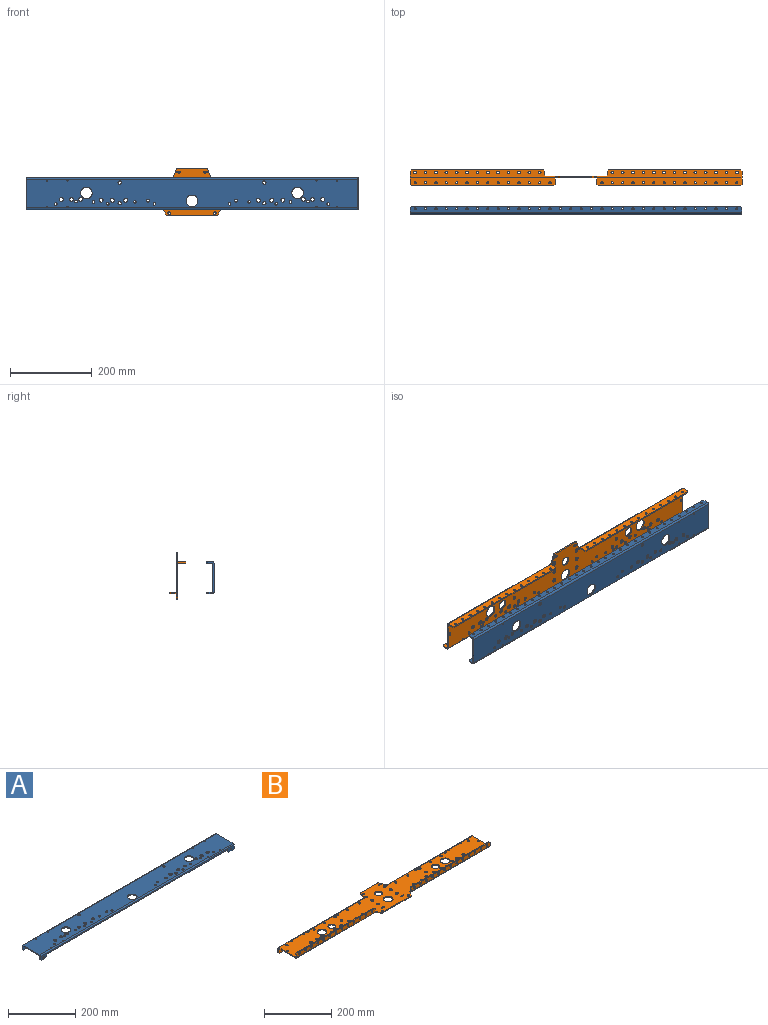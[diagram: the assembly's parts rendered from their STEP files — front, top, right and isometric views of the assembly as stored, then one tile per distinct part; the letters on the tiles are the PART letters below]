
ASSEMBLY  parts=2 mates=1
PART A: 101 faces, bbox 812.8x77.7x19.1 mm
  f0: cylinder r=4.06mm len=8.13mm, axis (0,0,1), area 81.1mm2, adj f83,f84
  f1: cylinder r=4.06mm len=8.13mm, axis (0,0,1), area 81.1mm2, adj f83,f84
  f2: cylinder r=4.06mm len=8.13mm, axis (0,0,1), area 81.1mm2, adj f83,f84
  f3: cylinder r=4.06mm len=8.13mm, axis (0,0,1), area 81.1mm2, adj f83,f84
  f4: cylinder r=3.38mm len=6.76mm, axis (0,0,1), area 67.4mm2, adj f83,f84
  f5: cylinder r=3.38mm len=6.76mm, axis (0,0,1), area 67.4mm2, adj f83,f84
  f6: cylinder r=3.38mm len=6.76mm, axis (0,0,1), area 67.4mm2, adj f83,f84
  f7: cylinder r=3.38mm len=6.76mm, axis (0,0,1), area 67.4mm2, adj f83,f84
  f8: cylinder r=3.35mm len=6.71mm, axis (0,0,1), area 66.9mm2, adj f83,f84
  f9: cylinder r=3.35mm len=6.71mm, axis (0,0,1), area 66.9mm2, adj f83,f84
  f10: cylinder r=3.35mm len=6.71mm, axis (0,0,1), area 66.9mm2, adj f83,f84
  f11: cylinder r=3.35mm len=6.71mm, axis (0,0,1), area 66.9mm2, adj f83,f84
  f12: cylinder r=3.35mm len=6.71mm, axis (0,0,1), area 66.9mm2, adj f83,f84
  f13: cylinder r=3.35mm len=6.71mm, axis (0,0,1), area 66.9mm2, adj f83,f84
  f14: cylinder r=3.35mm len=6.71mm, axis (0,0,1), area 66.9mm2, adj f83,f84
  f15: cylinder r=3.35mm len=6.71mm, axis (0,0,1), area 66.9mm2, adj f83,f84
  f16: cylinder r=3.35mm len=6.71mm, axis (0,0,1), area 66.9mm2, adj f83,f84
  f17: cylinder r=3.35mm len=6.71mm, axis (0,0,1), area 66.9mm2, adj f83,f84
  f18: cylinder r=14.29mm len=28.58mm, axis (0,0,1), area 285mm2, adj f83,f84
  f19: cylinder r=14.29mm len=28.58mm, axis (0,0,1), area 285mm2, adj f83,f84
  f20: cylinder r=1.27mm len=3.18mm, axis (0,0,1), area 25.3mm2, adj f83,f84
  f21: cylinder r=1.27mm len=3.18mm, axis (0,0,1), area 25.3mm2, adj f83,f84
  f22: cylinder r=1.27mm len=3.18mm, axis (0,0,1), area 25.3mm2, adj f83,f84
  f23: cylinder r=1.27mm len=3.18mm, axis (0,0,1), area 25.3mm2, adj f83,f84
  f24: cylinder r=1.27mm len=3.18mm, axis (0,0,1), area 25.3mm2, adj f83,f84
  f25: cylinder r=1.27mm len=3.18mm, axis (0,0,1), area 25.3mm2, adj f83,f84
  f26: cylinder r=1.27mm len=3.18mm, axis (0,0,1), area 25.3mm2, adj f83,f84
  f27: cylinder r=1.27mm len=3.18mm, axis (0,0,1), area 25.3mm2, adj f83,f84
  f28: cylinder r=4.83mm len=9.65mm, axis (0,0,1), area 96.3mm2, adj f83,f84
  f29: cylinder r=4.83mm len=9.65mm, axis (0,0,1), area 96.3mm2, adj f83,f84
  f30: cylinder r=4.83mm len=9.65mm, axis (0,0,1), area 96.3mm2, adj f83,f84
  f31: cylinder r=4.83mm len=9.65mm, axis (0,0,1), area 96.3mm2, adj f83,f84
  f32: cylinder r=4.83mm len=9.65mm, axis (0,0,1), area 96.3mm2, adj f83,f84
  f33: cylinder r=4.83mm len=9.65mm, axis (0,0,1), area 96.3mm2, adj f83,f84
  f34: cylinder r=4.83mm len=9.65mm, axis (0,0,1), area 96.3mm2, adj f83,f84
  f35: cylinder r=4.83mm len=9.65mm, axis (0,0,1), area 96.3mm2, adj f83,f84
  f36: cylinder r=4.83mm len=9.65mm, axis (0,0,1), area 96.3mm2, adj f83,f84
  f37: cylinder r=4.83mm len=9.65mm, axis (0,0,1), area 96.3mm2, adj f83,f84
  f38: cylinder r=4.83mm len=9.65mm, axis (0,0,1), area 96.3mm2, adj f83,f84
  f39: cylinder r=4.83mm len=9.65mm, axis (0,0,1), area 96.3mm2, adj f83,f84
  f40: cylinder r=2.67mm len=5.33mm, axis (0,1,0), area 53.2mm2, adj f75,f76
  f41: cylinder r=2.67mm len=5.33mm, axis (0,1,0), area 53.2mm2, adj f87,f88
  f42: cylinder r=2.67mm len=5.33mm, axis (0,1,0), area 53.2mm2, adj f87,f88
  f43: cylinder r=2.67mm len=5.33mm, axis (0,1,0), area 53.2mm2, adj f87,f88
  f44: cylinder r=2.67mm len=5.33mm, axis (0,1,0), area 53.2mm2, adj f87,f88
  f45: cylinder r=2.67mm len=5.33mm, axis (0,1,0), area 53.2mm2, adj f87,f88
  f46: cylinder r=2.67mm len=5.33mm, axis (0,1,0), area 53.2mm2, adj f87,f88
  f47: cylinder r=2.67mm len=5.33mm, axis (0,1,0), area 53.2mm2, adj f87,f88
  f48: cylinder r=2.67mm len=5.33mm, axis (0,1,0), area 53.2mm2, adj f87,f88
  f49: cylinder r=2.67mm len=5.33mm, axis (0,1,0), area 53.2mm2, adj f87,f88
  f50: cylinder r=2.67mm len=5.33mm, axis (0,1,0), area 53.2mm2, adj f87,f88
  f51: cylinder r=2.67mm len=5.33mm, axis (0,1,0), area 53.2mm2, adj f87,f88
  f52: cylinder r=2.67mm len=5.33mm, axis (0,1,0), area 53.2mm2, adj f87,f88
  f53: cylinder r=2.67mm len=5.33mm, axis (0,1,0), area 53.2mm2, adj f87,f88
  f54: cylinder r=2.67mm len=5.33mm, axis (0,1,0), area 53.2mm2, adj f87,f88
  f55: cylinder r=2.67mm len=5.33mm, axis (0,1,0), area 53.2mm2, adj f87,f88
  f56: cylinder r=2.67mm len=5.33mm, axis (0,1,0), area 53.2mm2, adj f87,f88
  f57: cylinder r=2.67mm len=5.33mm, axis (0,1,0), area 53.2mm2, adj f87,f88
  f58: cylinder r=2.67mm len=5.33mm, axis (0,1,0), area 53.2mm2, adj f87,f88
  f59: cylinder r=2.67mm len=5.33mm, axis (0,1,0), area 53.2mm2, adj f87,f88
  f60: cylinder r=2.67mm len=5.33mm, axis (0,1,0), area 53.2mm2, adj f87,f88
  f61: cylinder r=2.67mm len=5.33mm, axis (0,1,0), area 53.2mm2, adj f87,f88
  f62: cylinder r=2.67mm len=5.33mm, axis (0,1,0), area 53.2mm2, adj f87,f88
  f63: cylinder r=2.67mm len=5.33mm, axis (0,1,0), area 53.2mm2, adj f87,f88
  f64: cylinder r=2.67mm len=5.33mm, axis (0,1,0), area 53.2mm2, adj f87,f88
  f65: cylinder r=2.67mm len=5.33mm, axis (0,1,0), area 53.2mm2, adj f87,f88
  f66: cylinder r=2.67mm len=5.33mm, axis (0,1,0), area 53.2mm2, adj f87,f88
  f67: cylinder r=2.67mm len=5.33mm, axis (0,1,0), area 53.2mm2, adj f87,f88
  f68: cylinder r=2.67mm len=5.33mm, axis (0,1,0), area 53.2mm2, adj f87,f88
  f69: cylinder r=2.67mm len=5.33mm, axis (0,1,0), area 53.2mm2, adj f87,f88
  f70: cylinder r=2.67mm len=5.33mm, axis (0,1,0), area 53.2mm2, adj f87,f88
  f71: cylinder r=2.67mm len=5.33mm, axis (0,1,0), area 53.2mm2, adj f87,f88
  f72: cylinder r=2.67mm len=5.33mm, axis (0,1,0), area 53.2mm2, adj f75,f76
  f73: cylinder r=2.67mm len=5.33mm, axis (0,1,0), area 53.2mm2, adj f87,f88
  f74: cylinder r=14.29mm len=28.58mm, axis (0,0,1), area 285mm2, adj f83,f84
  f75: plane 812.8x15.11mm, normal (0,-1,0), area 3761.3mm2, adj f40,f72,f77,f79,f80,f81,f82,f90
  f76: plane 812.8x15.11mm, normal (0,1,0), area 3761.3mm2, adj f40,f72,f78,f79,f80,f81,f82,f90
  f77: cylinder r=3.94mm len=812.8mm, axis (-1,0,0), area 5026.5mm2, adj f75,f81,f82,f83
  f78: cylinder r=0.76mm len=812.8mm, axis (-1,0,0), area 972.9mm2, adj f76,f81,f82,f84
  f79: plane 19.05x3.18mm, normal (0,0,-1), area 60.5mm2, adj f75,f76,f91,f95
  f80: plane 19.05x3.18mm, normal (0,0,-1), area 60.5mm2, adj f75,f76,f90,f92
  f81: plane 77.72x15.88mm, normal (1,0,0), area 321mm2, adj f75,f76,f77,f78,f83,f84,f85,f86
  f82: plane 77.72x15.88mm, normal (-1,0,0), area 321mm2, adj f75,f76,f77,f78,f83,f84,f85,f86
  f83: plane 812.8x69.85mm, normal (0,0,1), area 53227.5mm2, adj f0,f1,f2,f3,f4,f5,f6,f7
  f84: plane 812.8x69.85mm, normal (0,0,-1), area 53227.5mm2, adj f0,f1,f2,f3,f4,f5,f6,f7
  f85: cylinder r=3.94mm len=812.8mm, axis (1,0,0), area 5026.5mm2, adj f81,f82,f83,f87
  f86: cylinder r=0.76mm len=812.8mm, axis (1,0,0), area 972.9mm2, adj f81,f82,f84,f88
  f87: plane 812.8x15.11mm, normal (0,1,0), area 11558.7mm2, adj f41,f42,f43,f44,f45,f46,f47,f48
  f88: plane 812.8x15.11mm, normal (0,-1,0), area 11558.7mm2, adj f41,f42,f43,f44,f45,f46,f47,f48
  f89: plane 806.45x3.18mm, normal (0,0,-1), area 2560.5mm2, adj f87,f88,f93,f94
  f90: plane 3.18x3.18mm, normal (-0.71,0,-0.71), area 14.3mm2, adj f75,f76,f80,f98
  f91: plane 3.18x3.18mm, normal (0.71,0,-0.71), area 14.3mm2, adj f75,f76,f79,f96
  f92: plane 3.18x3.18mm, normal (0.71,0,-0.71), area 14.3mm2, adj f75,f76,f80,f81
  f93: plane 3.18x3.18mm, normal (0.71,0,-0.71), area 14.3mm2, adj f81,f87,f88,f89
  f94: plane 3.18x3.18mm, normal (-0.71,0,-0.71), area 14.3mm2, adj f82,f87,f88,f89
  f95: plane 3.18x3.18mm, normal (-0.71,0,-0.71), area 14.3mm2, adj f75,f76,f79,f82
  f96: plane 4.76x3.18mm, normal (1,0,0), area 15.1mm2, adj f75,f76,f91,f100
  f97: plane 755.65x3.18mm, normal (0,0,-1), area 2399.2mm2, adj f75,f76,f99,f100
  f98: plane 4.76x3.18mm, normal (-1,0,0), area 15.1mm2, adj f75,f76,f90,f99
  f99: plane 3.18x3.18mm, normal (-0.71,0,-0.71), area 14.3mm2, adj f75,f76,f97,f98
  f100: plane 3.18x3.18mm, normal (0.71,0,-0.71), area 14.3mm2, adj f75,f76,f96,f97
PART B: 198 faces, bbox 812.8x116.3x38.1 mm
  f0: cylinder r=3.35mm len=6.71mm, axis (0,0,1), area 66.9mm2, adj f144,f145
  f1: cylinder r=3.35mm len=6.71mm, axis (0,0,1), area 66.9mm2, adj f144,f145
  f2: cylinder r=3.35mm len=6.71mm, axis (0,0,1), area 66.9mm2, adj f144,f145
  f3: cylinder r=3.35mm len=6.71mm, axis (0,0,1), area 66.9mm2, adj f144,f145
  f4: cylinder r=3.35mm len=6.71mm, axis (0,0,1), area 66.9mm2, adj f144,f145
  f5: cylinder r=3.35mm len=6.71mm, axis (0,0,1), area 66.9mm2, adj f144,f145
  f6: cylinder r=3.35mm len=6.71mm, axis (0,0,1), area 66.9mm2, adj f144,f145
  f7: cylinder r=3.35mm len=6.71mm, axis (0,0,1), area 66.9mm2, adj f144,f145
  f8: cylinder r=3.35mm len=6.71mm, axis (0,0,1), area 66.9mm2, adj f144,f145
  f9: cylinder r=3.35mm len=6.71mm, axis (0,0,1), area 66.9mm2, adj f144,f145
  f10: cylinder r=2.55mm len=5.11mm, axis (0,0,1), area 50.9mm2, adj f144,f145
  f11: cylinder r=1.79mm len=3.57mm, axis (0,0,1), area 35.6mm2, adj f144,f145
  f12: cylinder r=2.55mm len=5.11mm, axis (0,0,1), area 50.9mm2, adj f144,f145
  f13: cylinder r=1.79mm len=3.57mm, axis (0,0,1), area 35.6mm2, adj f144,f145
  f14: cylinder r=14.29mm len=28.58mm, axis (0,0,1), area 285mm2, adj f144,f145
  f15: cylinder r=4.06mm len=8.13mm, axis (0,0,1), area 81.1mm2, adj f144,f145
  f16: cylinder r=1.79mm len=3.57mm, axis (0,0,1), area 35.6mm2, adj f144,f145
  f17: cylinder r=2.55mm len=5.11mm, axis (0,0,1), area 50.9mm2, adj f144,f145
  f18: cylinder r=11.11mm len=22.23mm, axis (0,0,1), area 221.7mm2, adj f144,f145
  f19: cylinder r=4.06mm len=8.13mm, axis (0,0,1), area 81.1mm2, adj f144,f145
  f20: cylinder r=4.06mm len=8.13mm, axis (0,0,1), area 81.1mm2, adj f144,f145
  f21: cylinder r=1.79mm len=3.57mm, axis (0,0,1), area 35.6mm2, adj f144,f145
  f22: cylinder r=2.55mm len=5.11mm, axis (0,0,1), area 50.9mm2, adj f144,f145
  f23: cylinder r=2.55mm len=5.11mm, axis (0,0,1), area 50.9mm2, adj f144,f145
  f24: cylinder r=1.79mm len=3.57mm, axis (0,0,1), area 35.6mm2, adj f144,f145
  f25: cylinder r=2.55mm len=5.11mm, axis (0,0,1), area 50.9mm2, adj f144,f145
  f26: cylinder r=1.79mm len=3.57mm, axis (0,0,1), area 35.6mm2, adj f144,f145
  f27: cylinder r=4.06mm len=8.13mm, axis (0,0,1), area 81.1mm2, adj f144,f145
  f28: cylinder r=4.06mm len=8.13mm, axis (0,0,1), area 81.1mm2, adj f144,f145
  f29: cylinder r=4.06mm len=8.13mm, axis (0,0,1), area 81.1mm2, adj f144,f145
  f30: cylinder r=11.11mm len=22.23mm, axis (0,0,1), area 221.7mm2, adj f144,f145
  f31: cylinder r=1.79mm len=3.57mm, axis (0,0,1), area 35.6mm2, adj f144,f145
  f32: cylinder r=2.55mm len=5.11mm, axis (0,0,1), area 50.9mm2, adj f144,f145
  f33: cylinder r=14.29mm len=28.58mm, axis (0,0,1), area 285mm2, adj f144,f145
  f34: cylinder r=1.79mm len=3.57mm, axis (0,0,1), area 35.6mm2, adj f144,f145
  f35: cylinder r=2.55mm len=5.11mm, axis (0,0,1), area 50.9mm2, adj f144,f145
  f36: cylinder r=3.4mm len=6.81mm, axis (0,0,1), area 67.9mm2, adj f144,f145
  f37: cylinder r=3.4mm len=6.81mm, axis (0,0,1), area 67.9mm2, adj f144,f145
  f38: cylinder r=1.27mm len=3.18mm, axis (0,0,-1), area 25.3mm2, adj f144,f145
  f39: cylinder r=1.27mm len=3.18mm, axis (0,0,-1), area 25.3mm2, adj f144,f145
  f40: cylinder r=1.27mm len=3.18mm, axis (0,0,-1), area 25.3mm2, adj f144,f145
  f41: cylinder r=1.27mm len=3.18mm, axis (0,0,-1), area 25.3mm2, adj f144,f145
  f42: cylinder r=1.27mm len=3.18mm, axis (0,0,-1), area 25.3mm2, adj f144,f145
  f43: cylinder r=1.27mm len=3.18mm, axis (0,0,-1), area 25.3mm2, adj f144,f145
  f44: cylinder r=1.27mm len=3.18mm, axis (0,0,-1), area 25.3mm2, adj f144,f145
  f45: cylinder r=1.27mm len=3.18mm, axis (0,0,-1), area 25.3mm2, adj f144,f145
  f46: cylinder r=3.35mm len=6.71mm, axis (0,0,-1), area 66.9mm2, adj f144,f145
  f47: cylinder r=3.35mm len=6.71mm, axis (0,0,-1), area 66.9mm2, adj f144,f145
  f48: cylinder r=3.35mm len=6.71mm, axis (0,0,-1), area 66.9mm2, adj f144,f145
  f49: cylinder r=3.35mm len=6.71mm, axis (0,0,-1), area 66.9mm2, adj f144,f145
  f50: cylinder r=3.35mm len=6.71mm, axis (0,0,-1), area 66.9mm2, adj f144,f145
  f51: cylinder r=3.35mm len=6.71mm, axis (0,0,-1), area 66.9mm2, adj f144,f145
  f52: cylinder r=3.35mm len=6.71mm, axis (0,0,-1), area 66.9mm2, adj f144,f145
  f53: cylinder r=3.35mm len=6.71mm, axis (0,0,-1), area 66.9mm2, adj f144,f145
  f54: cylinder r=3.35mm len=6.71mm, axis (0,0,-1), area 66.9mm2, adj f144,f145
  f55: cylinder r=3.35mm len=6.71mm, axis (0,0,-1), area 66.9mm2, adj f144,f145
  f56: cylinder r=2.03mm len=4.06mm, axis (0,0,-1), area 40.5mm2, adj f144,f145
  f57: cylinder r=2.03mm len=4.06mm, axis (0,0,-1), area 40.5mm2, adj f144,f145
  f58: cylinder r=2.54mm len=5.08mm, axis (0,0,-1), area 50.7mm2, adj f144,f145
  f59: cylinder r=2.54mm len=5.08mm, axis (0,0,-1), area 50.7mm2, adj f144,f145
  f60: cylinder r=2.03mm len=4.06mm, axis (0,0,-1), area 40.5mm2, adj f144,f145
  f61: cylinder r=2.03mm len=4.06mm, axis (0,0,-1), area 40.5mm2, adj f144,f145
  f62: cylinder r=2.54mm len=5.08mm, axis (0,0,-1), area 50.7mm2, adj f144,f145
  f63: cylinder r=2.54mm len=5.08mm, axis (0,0,-1), area 50.7mm2, adj f144,f145
  f64: cylinder r=4.76mm len=9.53mm, axis (0,0,-1), area 95mm2, adj f144,f145
  f65: cylinder r=4.76mm len=9.53mm, axis (0,0,-1), area 95mm2, adj f144,f145
  f66: cylinder r=4.76mm len=9.53mm, axis (0,0,-1), area 95mm2, adj f144,f145
  f67: cylinder r=4.76mm len=9.53mm, axis (0,0,-1), area 95mm2, adj f144,f145
  f68: cylinder r=4.76mm len=9.53mm, axis (0,0,-1), area 95mm2, adj f144,f145
  f69: cylinder r=4.76mm len=9.53mm, axis (0,0,-1), area 95mm2, adj f144,f145
  f70: cylinder r=11.11mm len=22.23mm, axis (0,0,-1), area 221.7mm2, adj f144,f145
  f71: cylinder r=3.35mm len=6.71mm, axis (0,1,0), area 66.9mm2, adj f166,f167
  f72: cylinder r=3.35mm len=6.71mm, axis (0,1,0), area 66.9mm2, adj f166,f167
  f73: cylinder r=3.35mm len=6.71mm, axis (0,1,0), area 66.9mm2, adj f166,f167
  f74: cylinder r=3.35mm len=6.71mm, axis (0,1,0), area 66.9mm2, adj f166,f167
  f75: cylinder r=3.35mm len=6.71mm, axis (0,1,0), area 66.9mm2, adj f166,f167
  f76: cylinder r=3.35mm len=6.71mm, axis (0,1,0), area 66.9mm2, adj f166,f167
  f77: cylinder r=3.35mm len=6.71mm, axis (0,1,0), area 66.9mm2, adj f166,f167
  f78: cylinder r=3.35mm len=6.71mm, axis (0,1,0), area 66.9mm2, adj f166,f167
  f79: cylinder r=3.35mm len=6.71mm, axis (0,1,0), area 66.9mm2, adj f166,f167
  f80: cylinder r=3.35mm len=6.71mm, axis (0,1,0), area 66.9mm2, adj f166,f167
  f81: cylinder r=3.35mm len=6.71mm, axis (0,1,0), area 66.9mm2, adj f166,f167
  f82: cylinder r=3.35mm len=6.71mm, axis (0,1,0), area 66.9mm2, adj f166,f167
  f83: cylinder r=3.35mm len=6.71mm, axis (0,1,0), area 66.9mm2, adj f166,f167
  f84: cylinder r=3.35mm len=6.71mm, axis (0,1,0), area 66.9mm2, adj f159,f160
  f85: cylinder r=3.35mm len=6.71mm, axis (0,1,0), area 66.9mm2, adj f159,f160
  f86: cylinder r=3.35mm len=6.71mm, axis (0,1,0), area 66.9mm2, adj f159,f160
  f87: cylinder r=3.35mm len=6.71mm, axis (0,1,0), area 66.9mm2, adj f159,f160
  f88: cylinder r=3.35mm len=6.71mm, axis (0,1,0), area 66.9mm2, adj f159,f160
  f89: cylinder r=3.35mm len=6.71mm, axis (0,1,0), area 66.9mm2, adj f159,f160
  f90: cylinder r=3.35mm len=6.71mm, axis (0,1,0), area 66.9mm2, adj f159,f160
  f91: cylinder r=3.35mm len=6.71mm, axis (0,1,0), area 66.9mm2, adj f159,f160
  f92: cylinder r=3.35mm len=6.71mm, axis (0,1,0), area 66.9mm2, adj f159,f160
  f93: cylinder r=3.35mm len=6.71mm, axis (0,1,0), area 66.9mm2, adj f159,f160
  f94: cylinder r=3.35mm len=6.71mm, axis (0,1,0), area 66.9mm2, adj f159,f160
  f95: cylinder r=3.35mm len=6.71mm, axis (0,1,0), area 66.9mm2, adj f159,f160
  f96: cylinder r=3.35mm len=6.71mm, axis (0,1,0), area 66.9mm2, adj f159,f160
  f97: cylinder r=2.67mm len=5.33mm, axis (0,1,0), area 53.2mm2, adj f152,f153
  f98: cylinder r=2.67mm len=5.33mm, axis (0,1,0), area 53.2mm2, adj f152,f153
  f99: cylinder r=2.67mm len=5.33mm, axis (0,1,0), area 53.2mm2, adj f152,f153
  f100: cylinder r=2.67mm len=5.33mm, axis (0,1,0), area 53.2mm2, adj f152,f153
  f101: cylinder r=2.67mm len=5.33mm, axis (0,1,0), area 53.2mm2, adj f152,f153
  f102: cylinder r=2.67mm len=5.33mm, axis (0,1,0), area 53.2mm2, adj f152,f153
  f103: cylinder r=2.67mm len=5.33mm, axis (0,1,0), area 53.2mm2, adj f152,f153
  f104: cylinder r=2.67mm len=5.33mm, axis (0,1,0), area 53.2mm2, adj f152,f153
  f105: cylinder r=2.67mm len=5.33mm, axis (0,1,0), area 53.2mm2, adj f152,f153
  f106: cylinder r=2.67mm len=5.33mm, axis (0,1,0), area 53.2mm2, adj f152,f153
  f107: cylinder r=2.67mm len=5.33mm, axis (0,1,0), area 53.2mm2, adj f152,f153
  f108: cylinder r=2.67mm len=5.33mm, axis (0,1,0), area 53.2mm2, adj f152,f153
  f109: cylinder r=2.67mm len=5.33mm, axis (0,1,0), area 53.2mm2, adj f152,f153
  f110: cylinder r=2.67mm len=5.33mm, axis (0,1,0), area 53.2mm2, adj f152,f153
  f111: cylinder r=2.67mm len=5.33mm, axis (0,1,0), area 53.2mm2, adj f171,f172
  f112: cylinder r=2.67mm len=5.33mm, axis (0,1,0), area 53.2mm2, adj f171,f172
  f113: cylinder r=2.67mm len=5.33mm, axis (0,1,0), area 53.2mm2, adj f171,f172
  f114: cylinder r=2.67mm len=5.33mm, axis (0,1,0), area 53.2mm2, adj f171,f172
  f115: cylinder r=2.67mm len=5.33mm, axis (0,1,0), area 53.2mm2, adj f171,f172
  f116: cylinder r=2.67mm len=5.33mm, axis (0,1,0), area 53.2mm2, adj f171,f172
  f117: cylinder r=2.67mm len=5.33mm, axis (0,1,0), area 53.2mm2, adj f171,f172
  f118: cylinder r=2.67mm len=5.33mm, axis (0,1,0), area 53.2mm2, adj f171,f172
  f119: cylinder r=2.67mm len=5.33mm, axis (0,1,0), area 53.2mm2, adj f171,f172
  f120: cylinder r=2.67mm len=5.33mm, axis (0,1,0), area 53.2mm2, adj f171,f172
  f121: cylinder r=2.67mm len=5.33mm, axis (0,1,0), area 53.2mm2, adj f171,f172
  f122: cylinder r=2.67mm len=5.33mm, axis (0,1,0), area 53.2mm2, adj f171,f172
  f123: cylinder r=2.67mm len=5.33mm, axis (0,1,0), area 53.2mm2, adj f171,f172
  f124: cylinder r=2.67mm len=5.33mm, axis (0,1,0), area 53.2mm2, adj f171,f172
  f125: cylinder r=3.35mm len=6.71mm, axis (0,0,1), area 66.9mm2, adj f144,f145
  f126: cylinder r=3.35mm len=6.71mm, axis (0,0,1), area 66.9mm2, adj f144,f145
  f127: cylinder r=3.35mm len=6.71mm, axis (0,0,1), area 66.9mm2, adj f144,f145
  f128: cylinder r=3.35mm len=6.71mm, axis (0,0,1), area 66.9mm2, adj f144,f145
  f129: cylinder r=3.35mm len=6.71mm, axis (0,0,1), area 66.9mm2, adj f144,f145
  f130: cylinder r=3.35mm len=6.71mm, axis (0,0,1), area 66.9mm2, adj f144,f145
  f131: cylinder r=4.83mm len=9.65mm, axis (0,0,1), area 96.3mm2, adj f144,f145
  f132: cylinder r=4.83mm len=9.65mm, axis (0,0,1), area 96.3mm2, adj f144,f145
  f133: cylinder r=4.83mm len=9.65mm, axis (0,0,1), area 96.3mm2, adj f144,f145
  f134: cylinder r=4.83mm len=9.65mm, axis (0,0,1), area 96.3mm2, adj f144,f145
  f135: cylinder r=4.83mm len=9.65mm, axis (0,0,1), area 96.3mm2, adj f144,f145
  f136: cylinder r=4.83mm len=9.65mm, axis (0,0,1), area 96.3mm2, adj f144,f145
  f137: cylinder r=4.83mm len=9.65mm, axis (0,0,1), area 96.3mm2, adj f144,f145
  f138: cylinder r=4.83mm len=9.65mm, axis (0,0,1), area 96.3mm2, adj f144,f145
  f139: cylinder r=4.83mm len=9.65mm, axis (0,0,1), area 96.3mm2, adj f144,f145
  f140: cylinder r=4.83mm len=9.65mm, axis (0,0,1), area 96.3mm2, adj f144,f145
  f141: cylinder r=4.83mm len=9.65mm, axis (0,0,1), area 96.3mm2, adj f144,f145
  f142: cylinder r=4.83mm len=9.65mm, axis (0,0,1), area 96.3mm2, adj f144,f145
  f143: cylinder r=14.29mm len=28.58mm, axis (0,0,1), area 285mm2, adj f144,f145
  f144: plane 812.8x116.33mm, normal (0,0,1), area 55587.5mm2, adj f0,f1,f2,f3,f4,f5,f6,f7
  f145: plane 812.8x116.33mm, normal (0,0,-1), area 55587.5mm2, adj f0,f1,f2,f3,f4,f5,f6,f7
  f146: plane 71.83x3.18mm, normal (0,1,0), area 228.1mm2, adj f144,f145,f183,f184
  f147: plane 120.39x3.18mm, normal (0,-1,0), area 382.2mm2, adj f144,f145,f187,f189
  f148: plane 3.18x0.91mm, normal (0,1,0), area 2.9mm2, adj f144,f145,f176,f182
  f149: plane 3.18x0.91mm, normal (0,1,0), area 2.9mm2, adj f144,f145,f177,f185
  f150: cylinder r=3.94mm len=355.6mm, axis (1,0,0), area 2199.1mm2, adj f144,f152,f162,f176
  f151: cylinder r=0.76mm len=355.6mm, axis (1,0,0), area 425.6mm2, adj f145,f153,f162,f176
  f152: plane 355.6x18.29mm, normal (0,1,0), area 6180.3mm2, adj f97,f98,f99,f100,f101,f102,f103,f104
  f153: plane 355.6x18.29mm, normal (0,-1,0), area 6180.3mm2, adj f97,f98,f99,f100,f101,f102,f103,f104
  f154: plane 349.25x3.18mm, normal (0,0,-1), area 1108.9mm2, adj f152,f153,f195,f197
  f155: plane 3.18x1.34mm, normal (0,-1,0), area 4.3mm2, adj f144,f145,f174,f188
  f156: plane 3.18x1.34mm, normal (0,-1,0), area 4.3mm2, adj f144,f145,f175,f186
  f157: cylinder r=3.94mm len=330.2mm, axis (1,0,0), area 2042mm2, adj f145,f159,f163,f174
  f158: cylinder r=0.76mm len=330.2mm, axis (1,0,0), area 395.2mm2, adj f144,f160,f163,f174
  f159: plane 330.2x15.11mm, normal (0,-1,0), area 4521.1mm2, adj f84,f85,f86,f87,f88,f89,f90,f91
  f160: plane 330.2x15.11mm, normal (0,1,0), area 4521.1mm2, adj f84,f85,f86,f87,f88,f89,f90,f91
  f161: plane 323.85x3.18mm, normal (0,0,1), area 1028.2mm2, adj f159,f160,f191,f192
  f162: plane 77.72x31.75mm, normal (1,0,0), area 331.1mm2, adj f144,f145,f150,f151,f152,f153,f164,f165
  f163: plane 77.72x31.75mm, normal (-1,0,0), area 331.1mm2, adj f144,f145,f157,f158,f159,f160,f169,f170
  f164: cylinder r=3.94mm len=330.2mm, axis (1,0,0), area 2042mm2, adj f145,f162,f166,f175
  f165: cylinder r=0.76mm len=330.2mm, axis (1,0,0), area 395.2mm2, adj f144,f162,f167,f175
  f166: plane 330.2x15.11mm, normal (0,-1,0), area 4521.1mm2, adj f71,f72,f73,f74,f75,f76,f77,f78
  f167: plane 330.2x15.11mm, normal (0,1,0), area 4521.1mm2, adj f71,f72,f73,f74,f75,f76,f77,f78
  f168: plane 323.85x3.18mm, normal (0,0,1), area 1028.2mm2, adj f166,f167,f193,f194
  f169: cylinder r=3.94mm len=355.6mm, axis (1,0,0), area 2199.1mm2, adj f144,f163,f171,f177
  f170: cylinder r=0.76mm len=355.6mm, axis (1,0,0), area 425.6mm2, adj f145,f163,f172,f177
  f171: plane 355.6x18.29mm, normal (0,1,0), area 6180.3mm2, adj f111,f112,f113,f114,f115,f116,f117,f118
  f172: plane 355.6x18.29mm, normal (0,-1,0), area 6180.3mm2, adj f111,f112,f113,f114,f115,f116,f117,f118
  f173: plane 349.25x3.18mm, normal (0,0,-1), area 1108.9mm2, adj f171,f172,f190,f196
  f174: plane 15.88x3.94mm, normal (1,0,0), area 49.6mm2, adj f155,f157,f158,f159,f160,f192
  f175: plane 15.88x3.94mm, normal (-1,0,0), area 49.6mm2, adj f156,f164,f165,f166,f167,f193
  f176: plane 19.05x3.94mm, normal (-1,0,0), area 59.7mm2, adj f148,f150,f151,f152,f153,f197
  f177: plane 19.05x3.94mm, normal (1,0,0), area 59.7mm2, adj f149,f169,f170,f171,f172,f196
  f178: plane 15.88x9.17mm, normal (0.87,-0.5,0), area 58.2mm2, adj f144,f145,f186,f187
  f179: plane 15.88x9.17mm, normal (-0.87,-0.5,0), area 58.2mm2, adj f144,f145,f188,f189
  f180: plane 23.15x7.97mm, normal (-0.95,0.33,0), area 77.7mm2, adj f144,f145,f184,f185
  f181: plane 23.15x7.97mm, normal (0.95,0.33,0), area 77.7mm2, adj f144,f145,f182,f183
  f182: cylinder r=3.17mm len=3.18mm, axis (0,0,1), area 12.5mm2, adj f144,f145,f148,f181
  f183: cylinder r=3.17mm len=3.18mm, axis (0,0,-1), area 12.5mm2, adj f144,f145,f146,f181
  f184: cylinder r=3.17mm len=3.18mm, axis (0,0,-1), area 12.5mm2, adj f144,f145,f146,f180
  f185: cylinder r=3.17mm len=3.18mm, axis (0,0,-1), area 12.5mm2, adj f144,f145,f149,f180
  f186: cylinder r=3.17mm len=3.18mm, axis (0,0,-1), area 10.6mm2, adj f144,f145,f156,f178
  f187: cylinder r=3.17mm len=3.18mm, axis (0,0,-1), area 10.6mm2, adj f144,f145,f147,f178
  f188: cylinder r=3.17mm len=3.18mm, axis (0,0,1), area 10.6mm2, adj f144,f145,f155,f179
  f189: cylinder r=3.17mm len=3.18mm, axis (0,0,-1), area 10.6mm2, adj f144,f145,f147,f179
  f190: plane 3.18x3.18mm, normal (-0.71,0,-0.71), area 14.3mm2, adj f163,f171,f172,f173
  f191: plane 3.18x3.18mm, normal (-0.71,0,0.71), area 14.3mm2, adj f159,f160,f161,f163
  f192: plane 3.18x3.18mm, normal (0.71,0,0.71), area 14.3mm2, adj f159,f160,f161,f174
  f193: plane 3.18x3.18mm, normal (-0.71,0,0.71), area 14.3mm2, adj f166,f167,f168,f175
  f194: plane 3.18x3.18mm, normal (0.71,0,0.71), area 14.3mm2, adj f162,f166,f167,f168
  f195: plane 3.18x3.18mm, normal (0.71,0,-0.71), area 14.3mm2, adj f152,f153,f154,f162
  f196: plane 3.18x3.18mm, normal (0.71,0,-0.71), area 14.3mm2, adj f171,f172,f173,f177
  f197: plane 3.18x3.18mm, normal (-0.71,0,-0.71), area 14.3mm2, adj f152,f153,f154,f176
PLACE A rot(axis=(1,0,0),90deg) t=(-406.4,3.18,-17.27)mm
PLACE B rot(axis=(0,-0.71,-0.71),180deg) t=(406.4,88.9,-17.27)mm
MATE fastened A.f74 <-> B.f143  axis (0,1,0) through (0,3.18,0)mm
